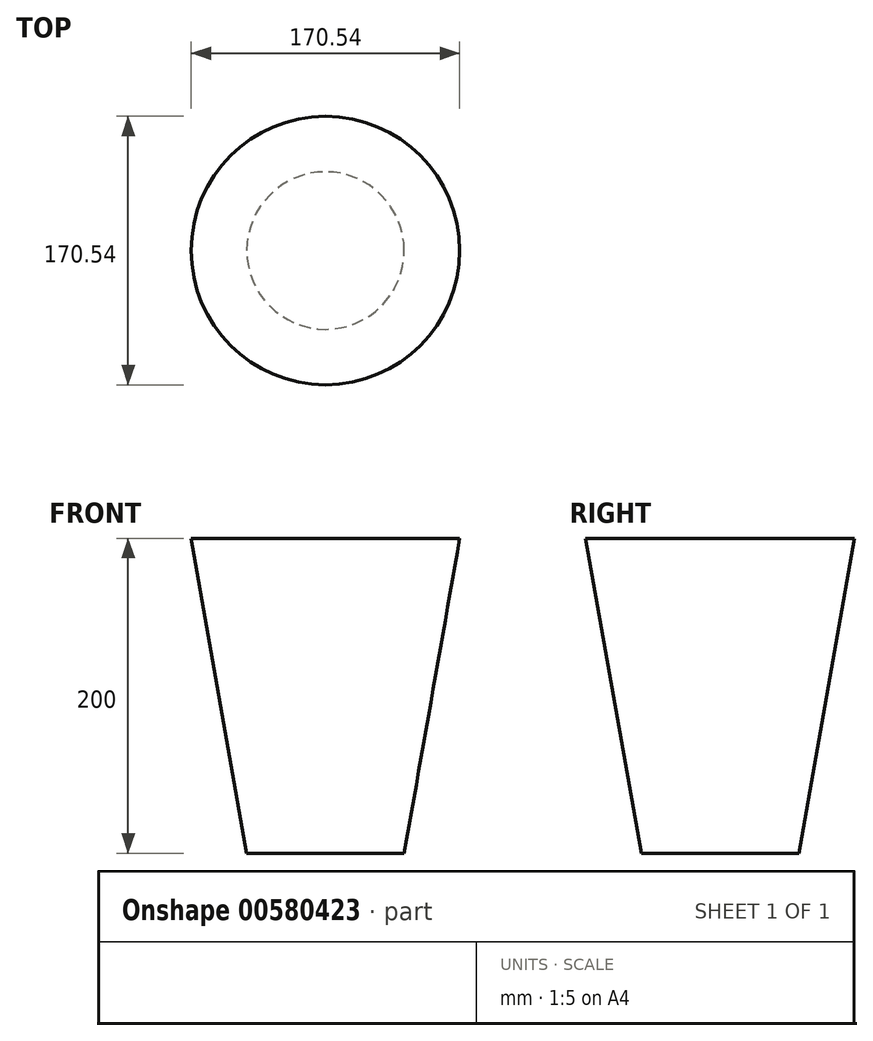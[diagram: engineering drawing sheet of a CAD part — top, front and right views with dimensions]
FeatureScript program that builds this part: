
annotation { "Feature Type Name" : "Feature", "Feature Type Description" : "" }
export const myFeature = defineFeature(function(context is Context, id is Id, definition is map)
    precondition{}
    {
        {
            var Q0;
            Q0=qCreatedBy(makeId("Top.planeOp"),FACE);
            var sketch = newSketch(context, id + "F0", { "sketchPlane" : qUnion([Q0])});
            skCircle(sketch, "E0", {"center": v(0, 0) * mm, "radius": 50 * mm});
            skSolve(sketch);
        }
        {
            var Q0;
            Q0=makeQuery(id+"F0.imprint","IMPRINT",FACE,{"disambiguationData":[TD([[makeQuery(id+"F0.imprint","IMPRINT",EDGE,{"derivedFrom":sQuery(id+"F0.wireOp",EDGE,"E0")}),1.0]])]});
            extrude(context, id + "F1", {"entities" : qUnion([Q0]), "depth" : 200 * mm, "offsetDistance" : 25 * mm, "hasDraft" : true, "draftAngle" : 10 * degree});
        }
    });
